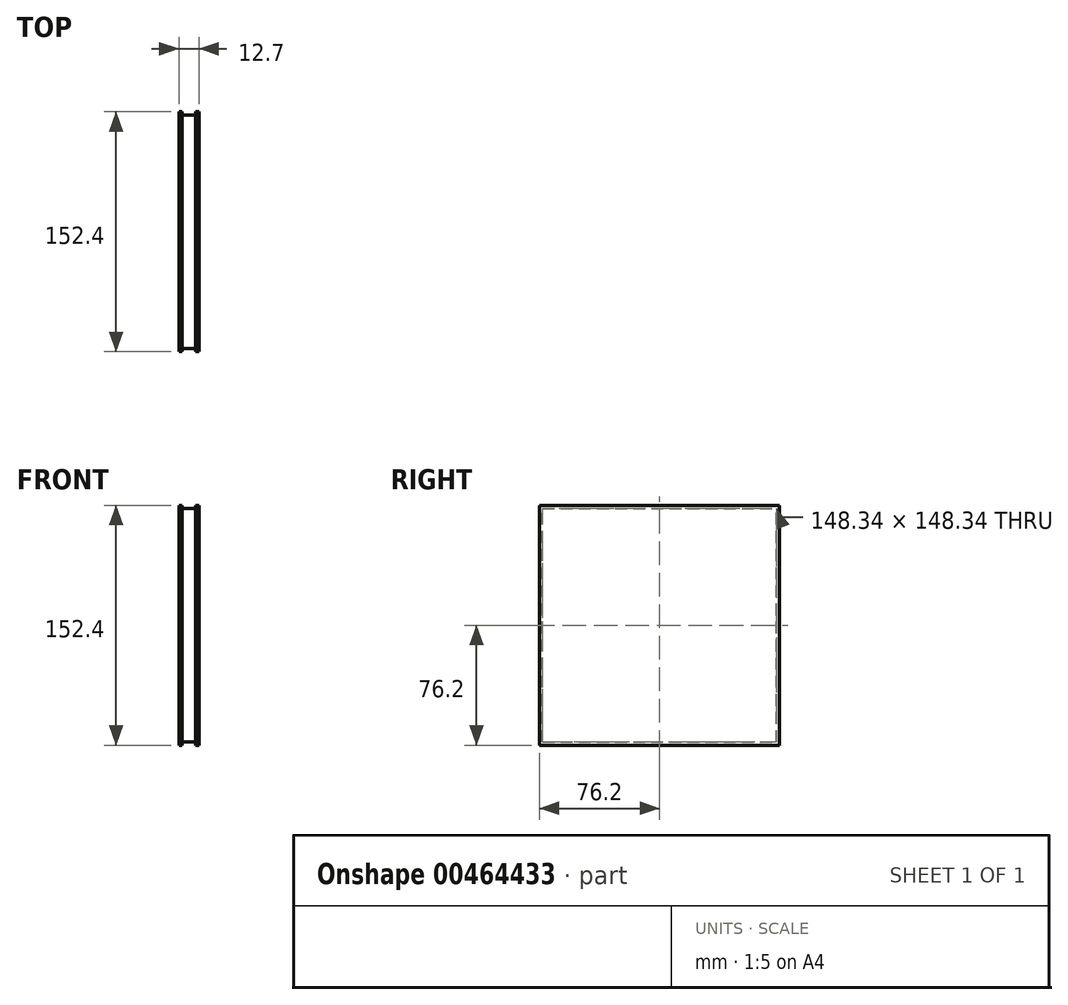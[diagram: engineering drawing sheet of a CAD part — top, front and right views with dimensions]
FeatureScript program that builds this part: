
annotation { "Feature Type Name" : "Feature", "Feature Type Description" : "" }
export const myFeature = defineFeature(function(context is Context, id is Id, definition is map)
    precondition{}
    {
        {
            var Q0;
            Q0=qCreatedBy(makeId("Right.planeOp"),FACE);
            var sketch = newSketch(context, id + "F0", { "sketchPlane" : qUnion([Q0])});
            skLineSegment(sketch, "E0.bottom", {"start": v(0, 0) * mm, "end": v(152.4, 0) * mm});
            skLineSegment(sketch, "E0.top", {"start": v(0, 152.4) * mm, "end": v(152.4, 152.4) * mm});
            skLineSegment(sketch, "E0.left", {"start": v(0, 0) * mm, "end": v(0, 152.4) * mm});
            skLineSegment(sketch, "E0.right", {"start": v(152.4, 0) * mm, "end": v(152.4, 152.4) * mm});
            skSolve(sketch);
        }
        {
            var Q0;
            Q0=makeQuery(id+"F0.imprint","IMPRINT",FACE,{"disambiguationData":[TD([[makeQuery(id+"F0.imprint","IMPRINT",EDGE,{"derivedFrom":sQuery(id+"F0.wireOp",EDGE,"E0.bottom")}),1.0]])]});
            extrude(context, id + "F1", {"entities" : qUnion([Q0]), "depth" : 2.03 * mm});
        }
        {
            var Q0;
            Q0=makeQuery(id+"F1.opExtrude","CAP_FACE",FACE,{"disambiguationData":[OSD([sQuery(id+"F0.wireOp",EDGE,"E0.bottom"),sQuery(id+"F0.wireOp",EDGE,"E0.top"),sQuery(id+"F0.wireOp",EDGE,"E0.left"),sQuery(id+"F0.wireOp",EDGE,"E0.right")])],"isStart":false});
            var sketch = newSketch(context, id + "F2", { "sketchPlane" : qUnion([Q0])});
            skLineSegment(sketch, "E1", {"start": v(0, 0) * mm, "end": v(2.03, 0) * mm});
            skLineSegment(sketch, "E2", {"start": v(2.03, 0) * mm, "end": v(2.03, 2.03) * mm});
            skLineSegment(sketch, "E3.bottom", {"start": v(2.03, 2.03) * mm, "end": v(150.37, 2.03) * mm});
            skLineSegment(sketch, "E3.top", {"start": v(2.03, 150.37) * mm, "end": v(150.37, 150.37) * mm});
            skLineSegment(sketch, "E3.left", {"start": v(2.03, 2.03) * mm, "end": v(2.03, 150.37) * mm});
            skLineSegment(sketch, "E3.right", {"start": v(150.37, 2.03) * mm, "end": v(150.37, 150.37) * mm});
            skSolve(sketch);
        }
        {
            var Q0;
            Q0=makeQuery(id+"F2.imprint","IMPRINT",FACE,{"disambiguationData":[TD([[makeQuery(id+"F2.imprint","IMPRINT",EDGE,{"derivedFrom":sQuery(id+"F2.wireOp",EDGE,"E3.bottom")}),1.0]])]});
            extrude(context, id + "F3", {"entities" : qUnion([Q0]), "operationType" : NewBodyOperationType.ADD, "depth" : 8.64 * mm});
        }
        {
            var Q0;
            Q0=makeQuery(id+"F3.opExtrude","CAP_FACE",FACE,{"disambiguationData":[OSD([sQuery(id+"F2.wireOp",EDGE,"E3.bottom"),sQuery(id+"F2.wireOp",EDGE,"E3.top"),sQuery(id+"F2.wireOp",EDGE,"E3.left"),sQuery(id+"F2.wireOp",EDGE,"E3.right")])],"isStart":false});
            var sketch = newSketch(context, id + "F4", { "sketchPlane" : qUnion([Q0])});
            skLineSegment(sketch, "E4", {"start": v(2.03, 2.03) * mm, "end": v(0, 2.03) * mm});
            skLineSegment(sketch, "E5", {"start": v(0, 2.03) * mm, "end": v(0, 0) * mm});
            skLineSegment(sketch, "E6.bottom", {"start": v(0, 0) * mm, "end": v(152.4, 0) * mm});
            skLineSegment(sketch, "E6.top", {"start": v(0, 152.4) * mm, "end": v(152.4, 152.4) * mm});
            skLineSegment(sketch, "E6.left", {"start": v(0, 0) * mm, "end": v(0, 152.4) * mm});
            skLineSegment(sketch, "E6.right", {"start": v(152.4, 0) * mm, "end": v(152.4, 152.4) * mm});
            skSolve(sketch);
        }
        {
            var Q0;
            {var subQ3=sQuery(id+"F4.wireOp",EDGE,"E6.bottom");Q0=makeQuery(id+"F4.imprint","IMPRINT",FACE,{"disambiguationData":[TD([[makeQuery(id+"F4.imprint","IMPRINT",EDGE,{"derivedFrom":subQ3}),1.0]])]});}
            var Q1;
            Q1=makeQuery(id+"F4.imprint","IMPRINT",FACE,{"disambiguationData":[TD([[makeQuery(id+"F4.imprint","IMPRINT",EDGE,{"derivedFrom":makeQuery(id+"F3.opExtrude","CAP_EDGE",EDGE,{"disambiguationData":[OSD([sQuery(id+"F2.wireOp",EDGE,"E3.bottom")])],"isStart":false})}),1.0]])]});
            extrude(context, id + "F5", {"entities" : qUnion([Q0, Q1]), "operationType" : NewBodyOperationType.ADD, "depth" : 2.03 * mm});
        }
    });
